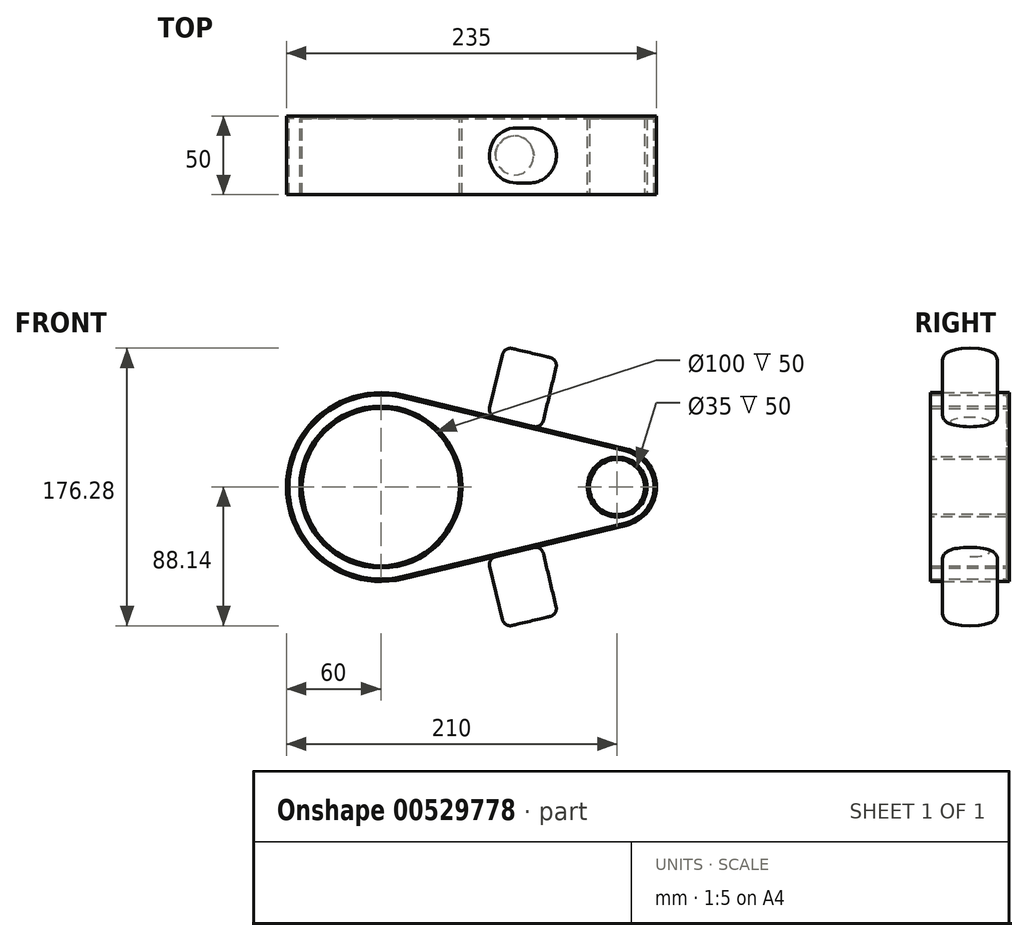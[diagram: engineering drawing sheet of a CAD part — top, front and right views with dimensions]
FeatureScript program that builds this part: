
annotation { "Feature Type Name" : "Feature", "Feature Type Description" : "" }
export const myFeature = defineFeature(function(context is Context, id is Id, definition is map)
    precondition{}
    {
        {
            var Q0;
            Q0=qCreatedBy(makeId("Front.planeOp"),FACE);
            var sketch = newSketch(context, id + "F0", { "sketchPlane" : qUnion([Q0])});
            skCircle(sketch, "E0", {"center": v(0, 0) * mm, "radius": 60 * mm});
            skCircle(sketch, "E1", {"center": v(150, 0) * mm, "radius": 25 * mm});
            skLineSegment(sketch, "E2", {"start": v(14, 58.34) * mm, "end": v(155.83, 24.3) * mm});
            skLineSegment(sketch, "E3", {"start": v(14, -58.34) * mm, "end": v(155.83, -24.3) * mm});
            skCircle(sketch, "E4", {"center": v(0, 0) * mm, "radius": 50 * mm});
            skSolve(sketch);
        }
        {
            var Q0;
            Q0 = qSketchRegion(id + "F0", true);
            extrude(context, id + "F1", {"entities" : qUnion([Q0]), "depth" : 50 * mm, "offsetDistance" : 25 * mm});
        }
        {
            var Q0;
            Q0=makeQuery(id+"F1.opExtrude","SWEPT_FACE",FACE,{"disambiguationData":[OSD([sQuery(id+"F0.wireOp",EDGE,"E2")])]});
            var sketch = newSketch(context, id + "F2", { "sketchPlane" : qUnion([Q0])});
            skCircle(sketch, "E5", {"center": v(72.93, -25) * mm, "radius": 17.5 * mm});
            skPoint(sketch, "E5.centerSnap0", {"position": v(145.86, -25) * mm});
            skPoint(sketch, "E5.centerSnap1", {"position": v(72.93, 0) * mm});
            skSolve(sketch);
        }
        {
            var Q0;
            Q0 = qSketchRegion(id + "F2", true);
            extrude(context, id + "F3", {"entities" : qUnion([Q0]), "depth" : 45 * mm, "offsetDistance" : 25 * mm});
        }
        {
            var Q0;
            Q0=makeQuery(id+"F3.opExtrude","CAP_EDGE",EDGE,{"disambiguationData":[OSD([sQuery(id+"F2.wireOp",EDGE,"E5")])],"isStart":false});
            var Q1;
            Q1=makeQuery(id+"F3.opExtrude","CAP_EDGE",EDGE,{"disambiguationData":[OSD([sQuery(id+"F2.wireOp",EDGE,"E5")])],"isStart":true});
            fillet(context, id + "F4", {"entities" : qUnion([Q0, Q1]), "radius" : 5 * mm, "tangentPropagation" : true, "allowEdgeOverflow" : false});
        }
        {
            var Q0;
            Q0=makeQuery(id+"F1.opExtrude","CAP_FACE",FACE,{"disambiguationData":[OSD([sQuery(id+"F0.wireOp",EDGE,"E0"),sQuery(id+"F0.wireOp",EDGE,"E1"),sQuery(id+"F0.wireOp",EDGE,"E2"),sQuery(id+"F0.wireOp",EDGE,"E3"),sQuery(id+"F0.wireOp",EDGE,"E4")])],"isStart":false});
            var sketch = newSketch(context, id + "F5", { "sketchPlane" : qUnion([Q0])});
            skCircle(sketch, "E6", {"center": v(150, 0) * mm, "radius": 17.5 * mm});
            skSolve(sketch);
        }
        {
            var Q0;
            Q0 = qSketchRegion(id + "F5", true);
            extrude(context, id + "F6", {"entities" : qUnion([Q0]), "operationType" : NewBodyOperationType.REMOVE, "endBound" : BoundingType.THROUGH_ALL, "oppositeDirection" : true, "depth" : 25 * mm, "offsetDistance" : 25 * mm});
        }
        {
            var Q0;
            Q0=makeQuery(id+"F1.opExtrude","CAP_FACE",FACE,{"disambiguationData":[OSD([sQuery(id+"F0.wireOp",EDGE,"E0"),sQuery(id+"F0.wireOp",EDGE,"E1"),sQuery(id+"F0.wireOp",EDGE,"E2"),sQuery(id+"F0.wireOp",EDGE,"E3"),sQuery(id+"F0.wireOp",EDGE,"E4")])],"isStart":false});
            shell(context, id + "F7", {"entities" : qUnion([Q0]), "thickness" : 1.5 * mm});
        }
        {
            var Q0;
            Q0=makeQuery(id+"F3.opExtrude","SWEPT_BODY",BODY,{"disambiguationData":[OSD([sQuery(id+"F2.wireOp",EDGE,"E5")])]});
            var Q1;
            Q1=qCreatedBy(makeId("Top.planeOp"),FACE);
            mirror(context, id + "F8", {"operationType" : NewBodyOperationType.ADD, "entities" : qUnion([Q0]), "mirrorPlane" : qUnion([Q1])});
        }
    });
